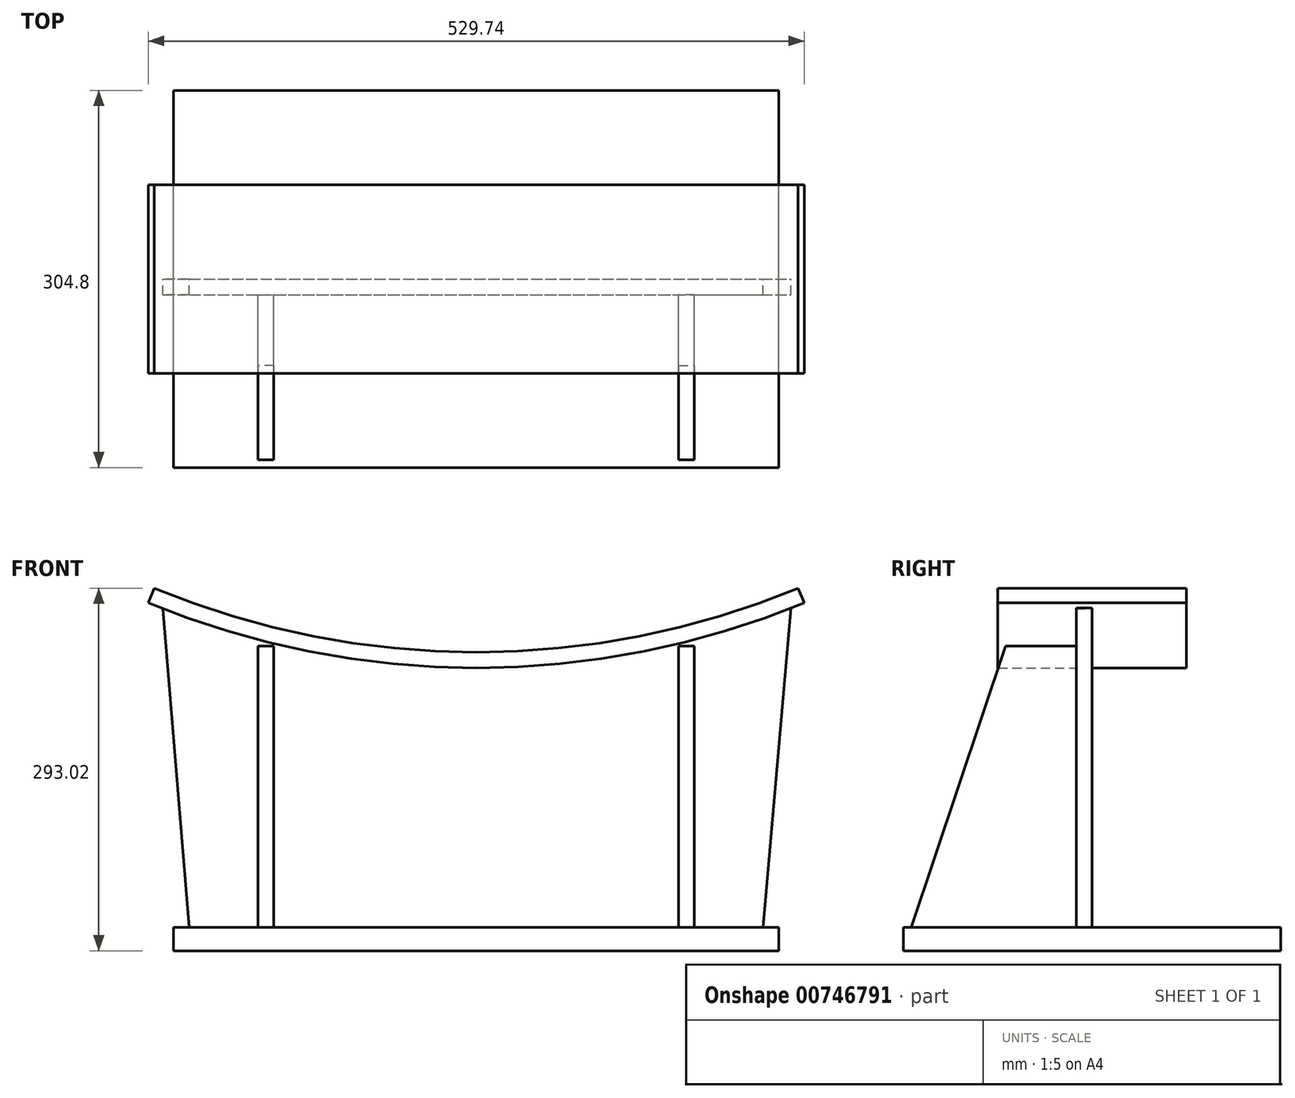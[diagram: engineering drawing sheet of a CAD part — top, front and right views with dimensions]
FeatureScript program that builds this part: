
annotation { "Feature Type Name" : "Feature", "Feature Type Description" : "" }
export const myFeature = defineFeature(function(context is Context, id is Id, definition is map)
    precondition{}
    {
        {
            var Q0;
            Q0=qCreatedBy(makeId("Front.planeOp"),FACE);
            var sketch = newSketch(context, id + "F0", { "sketchPlane" : qUnion([Q0])});
            skArc(sketch, "E0", {"start": v(-260.01, -699.63) * mm, "mid": v(0, -751.35) * mm, "end": v(260.01, -699.63) * mm});
            skArc(sketch, "E1", {"start": v(-264.87, -711.36) * mm, "mid": v(0.58, -764.05) * mm, "end": v(265.95, -710.91) * mm});
            skLineSegment(sketch, "E2", {"start": v(-260.01, -699.63) * mm, "end": v(-264.87, -711.36) * mm});
            skLineSegment(sketch, "E3.MirrorCS", {"start": v(260.01, -699.63) * mm, "end": v(264.87, -711.36) * mm});
            skLineSegment(sketch, "E4", {"start": v(-264.62, -710.74) * mm, "end": v(-253.1, -716.1) * mm, "construction": true});
            skLineSegment(sketch, "E5", {"start": v(265.95, -710.91) * mm, "end": v(254.18, -715.68) * mm, "construction": true});
            skLineSegment(sketch, "E6.bottom", {"start": v(244.47, -992.65) * mm, "end": v(-244.48, -992.65) * mm});
            skLineSegment(sketch, "E6.left", {"start": v(244.47, -992.65) * mm, "end": v(244.47, -973.6) * mm});
            skLineSegment(sketch, "E6.right", {"start": v(-244.48, -992.65) * mm, "end": v(-244.48, -973.6) * mm});
            skPoint(sketch, "E6.middle", {"position": v(0, -878.35) * mm});
            skLineSegment(sketch, "E7", {"start": v(-244.48, -973.6) * mm, "end": v(244.47, -973.6) * mm});
            skLineSegment(sketch, "E8", {"start": v(-244.48, -973.6) * mm, "end": v(-231.78, -973.6) * mm, "construction": true});
            skLineSegment(sketch, "E9", {"start": v(244.47, -973.6) * mm, "end": v(231.77, -973.6) * mm, "construction": true});
            skLineSegment(sketch, "E10", {"start": v(-231.78, -973.6) * mm, "end": v(-253.1, -716.1) * mm});
            skLineSegment(sketch, "E11", {"start": v(231.77, -973.6) * mm, "end": v(254.18, -715.68) * mm});
            skPoint(sketch, "E12.orphan", {"position": v(-244.48, -764.05) * mm});
            skPoint(sketch, "E13.orphan", {"position": v(244.48, -764.05) * mm});
            skSolve(sketch);
        }
        {
            var Q0;
            Q0=makeQuery(id+"F0.imprint","IMPRINT",FACE,{"disambiguationData":[TD([[makeQuery(id+"F0.imprint","IMPRINT",EDGE,{"derivedFrom":sQuery(id+"F0.wireOp",EDGE,"E6.bottom")}),-1.0]])]});
            extrude(context, id + "F1", {"entities" : qUnion([Q0]), "depth" : 304.8 * mm, "offsetDistance" : 25.4 * mm, "symmetric" : true});
        }
        {
            var Q0;
            Q0 = qSketchRegion(id + "F0", true);
            extrude(context, id + "F2", {"entities" : qUnion([Q0]), "operationType" : NewBodyOperationType.ADD, "depth" : 12.7 * mm, "offsetDistance" : 25.4 * mm});
        }
        {
            var Q0;
            Q0=makeQuery(id+"F0.imprint","IMPRINT",FACE,{"disambiguationData":[TD([[makeQuery(id+"F0.imprint","IMPRINT",EDGE,{"derivedFrom":sQuery(id+"F0.wireOp",EDGE,"E0")}),-1.0]])]});
            extrude(context, id + "F3", {"entities" : qUnion([Q0]), "operationType" : NewBodyOperationType.ADD, "depth" : 152.4 * mm, "offsetDistance" : 25.4 * mm, "symmetric" : true});
        }
        {
            var Q0;
            Q0=makeQuery(id+"F2.opExtrude","CAP_FACE",FACE,{"disambiguationData":[OSD([sQuery(id+"F0.wireOp",EDGE,"E0"),sQuery(id+"F0.wireOp",EDGE,"E1"),sQuery(id+"F0.wireOp",EDGE,"E2"),sQuery(id+"F0.wireOp",EDGE,"E3.MirrorCS"),sQuery(id+"F0.wireOp",EDGE,"E6.bottom"),sQuery(id+"F0.wireOp",EDGE,"E6.left"),sQuery(id+"F0.wireOp",EDGE,"E6.right"),sQuery(id+"F0.wireOp",EDGE,"E7"),sQuery(id+"F0.wireOp",EDGE,"E10"),sQuery(id+"F0.wireOp",EDGE,"E11")])],"isStart":false});
            var sketch = newSketch(context, id + "F4", { "sketchPlane" : qUnion([Q0])});
            skLineSegment(sketch, "E14.bottom", {"start": v(-176.21, -973.6) * mm, "end": v(-163.51, -973.6) * mm});
            skLineSegment(sketch, "E14.left", {"start": v(-176.21, -973.6) * mm, "end": v(-176.21, -746.27) * mm});
            skLineSegment(sketch, "E14.right", {"start": v(-163.51, -973.6) * mm, "end": v(-163.51, -746.27) * mm});
            skLineSegment(sketch, "E15.MirrorCS", {"start": v(163.51, -973.6) * mm, "end": v(163.51, -746.27) * mm});
            skLineSegment(sketch, "E16.MirrorCS", {"start": v(176.21, -973.6) * mm, "end": v(176.21, -746.27) * mm});
            skLineSegment(sketch, "E17.MirrorCS", {"start": v(176.21, -973.6) * mm, "end": v(163.51, -973.6) * mm});
            skLineSegment(sketch, "E18", {"start": v(-176.21, -746.27) * mm, "end": v(-163.51, -746.27) * mm});
            skPoint(sketch, "E19.orphan", {"position": v(-163.51, -744.46) * mm});
            skPoint(sketch, "E20.orphan", {"position": v(-176.21, -742.88) * mm});
            skLineSegment(sketch, "E21.MirrorCS", {"start": v(176.21, -746.27) * mm, "end": v(163.51, -746.27) * mm});
            skPoint(sketch, "E22.MirrorCS.end.orphan", {"position": v(163.51, -744.46) * mm});
            skPoint(sketch, "E22.MirrorCS.start.orphan", {"position": v(176.21, -742.88) * mm});
            skSolve(sketch);
        }
        {
            var Q0;
            Q0=makeQuery(id+"F4.imprint","IMPRINT",FACE,{"disambiguationData":[TD([[makeQuery(id+"F4.imprint","IMPRINT",EDGE,{"derivedFrom":sQuery(id+"F4.wireOp",EDGE,"E14.bottom")}),1.0]])]});
            var Q1;
            Q1=makeQuery(id+"F4.imprint","IMPRINT",FACE,{"disambiguationData":[TD([[makeQuery(id+"F4.imprint","IMPRINT",EDGE,{"derivedFrom":sQuery(id+"F4.wireOp",EDGE,"E15.MirrorCS")}),-1.0]])]});
            extrude(context, id + "F5", {"entities" : qUnion([Q0, Q1]), "operationType" : NewBodyOperationType.ADD, "depth" : 25.4 * mm, "offsetDistance" : 25.4 * mm});
        }
        {
            var Q0;
            Q0 = qSketchRegion(id + "F4", true);
            extrude(context, id + "F6", {"entities" : qUnion([Q0]), "operationType" : NewBodyOperationType.ADD, "depth" : 133.35 * mm, "offsetDistance" : 25.4 * mm});
        }
        {
            var Q0;
            {var subQ0=sQuery(id+"F4.wireOp",EDGE,"E14.left");Q0=makeQuery(id+"F6.boolean.opBoolean","MERGE",FACE,{"derivedFrom":[makeQuery(id+"F5.opExtrude","SWEPT_FACE",FACE,{"disambiguationData":[OSD([subQ0])]}),makeQuery(id+"F6.opExtrude","SWEPT_FACE",FACE,{"disambiguationData":[OSD([subQ0])]})]});}
            var sketch = newSketch(context, id + "F7", { "sketchPlane" : qUnion([Q0])});
            skLineSegment(sketch, "E23", {"start": v(12.7, -746.27) * mm, "end": v(69.85, -746.27) * mm, "construction": true});
            skLineSegment(sketch, "E24", {"start": v(69.85, -746.27) * mm, "end": v(146.05, -973.6) * mm});
            skSolve(sketch);
        }
        {
            var Q0;
            {var subQ0=sQuery(id+"F7.wireOp",EDGE,"E24");Q0=makeQuery(id+"F7.imprint","IMPRINT",FACE,{"disambiguationData":[TD([[makeQuery(id+"F7.imprint","IMPRINT",EDGE,{"derivedFrom":subQ0}),1.0]])]});}
            extrude(context, id + "F8", {"entities" : qUnion([Q0]), "operationType" : NewBodyOperationType.REMOVE, "oppositeDirection" : true, "depth" : 12.7 * mm, "offsetDistance" : 25.4 * mm});
        }
        {
            var Q0;
            {var subQ0=sQuery(id+"F4.wireOp",EDGE,"E16.MirrorCS");Q0=makeQuery(id+"F6.boolean.opBoolean","MERGE",FACE,{"derivedFrom":[makeQuery(id+"F5.opExtrude","SWEPT_FACE",FACE,{"disambiguationData":[OSD([subQ0])]}),makeQuery(id+"F6.opExtrude","SWEPT_FACE",FACE,{"disambiguationData":[OSD([subQ0])]})]});}
            var sketch = newSketch(context, id + "F9", { "sketchPlane" : qUnion([Q0])});
            skLineSegment(sketch, "E25", {"start": v(-12.7, -746.27) * mm, "end": v(-69.85, -746.27) * mm, "construction": true});
            skLineSegment(sketch, "E26", {"start": v(-69.85, -746.27) * mm, "end": v(-146.05, -973.6) * mm});
            skSolve(sketch);
        }
        {
            var Q0;
            {var subQ0=sQuery(id+"F9.wireOp",EDGE,"E26");Q0=makeQuery(id+"F9.imprint","IMPRINT",FACE,{"disambiguationData":[TD([[makeQuery(id+"F9.imprint","IMPRINT",EDGE,{"derivedFrom":subQ0}),-1.0]])]});}
            extrude(context, id + "F10", {"entities" : qUnion([Q0]), "operationType" : NewBodyOperationType.REMOVE, "oppositeDirection" : true, "depth" : 12.7 * mm, "offsetDistance" : 25.4 * mm});
        }
    });
